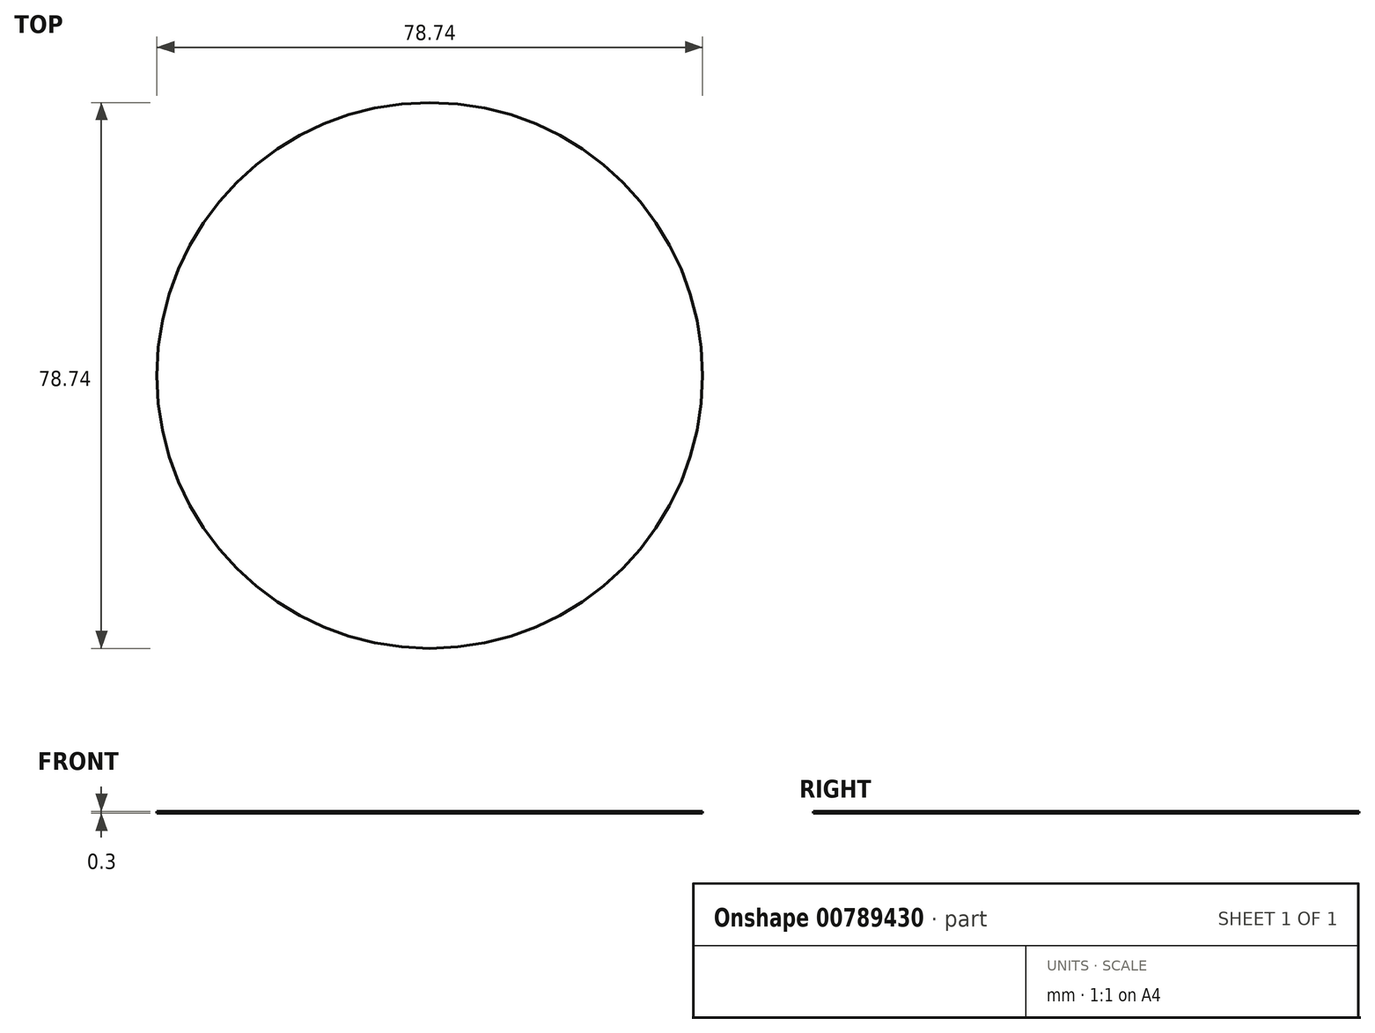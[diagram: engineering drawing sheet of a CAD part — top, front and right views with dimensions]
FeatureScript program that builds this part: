
annotation { "Feature Type Name" : "Feature", "Feature Type Description" : "" }
export const myFeature = defineFeature(function(context is Context, id is Id, definition is map)
    precondition{}
    {
        {
            var Q0;
            Q0=qCreatedBy(makeId("Top.planeOp"),FACE);
            var sketch = newSketch(context, id + "F0", { "sketchPlane" : qUnion([Q0])});
            skCircle(sketch, "E0", {"center": v(0, 0) * mm, "radius": 39.37 * mm});
            skSolve(sketch);
        }
        {
            var Q0;
            Q0 = qSketchRegion(id + "F0", true);
            extrude(context, id + "F1", {"entities" : qUnion([Q0]), "oppositeDirection" : true, "depth" : 0.3 * mm, "offsetDistance" : 25.4 * mm});
        }
    });
